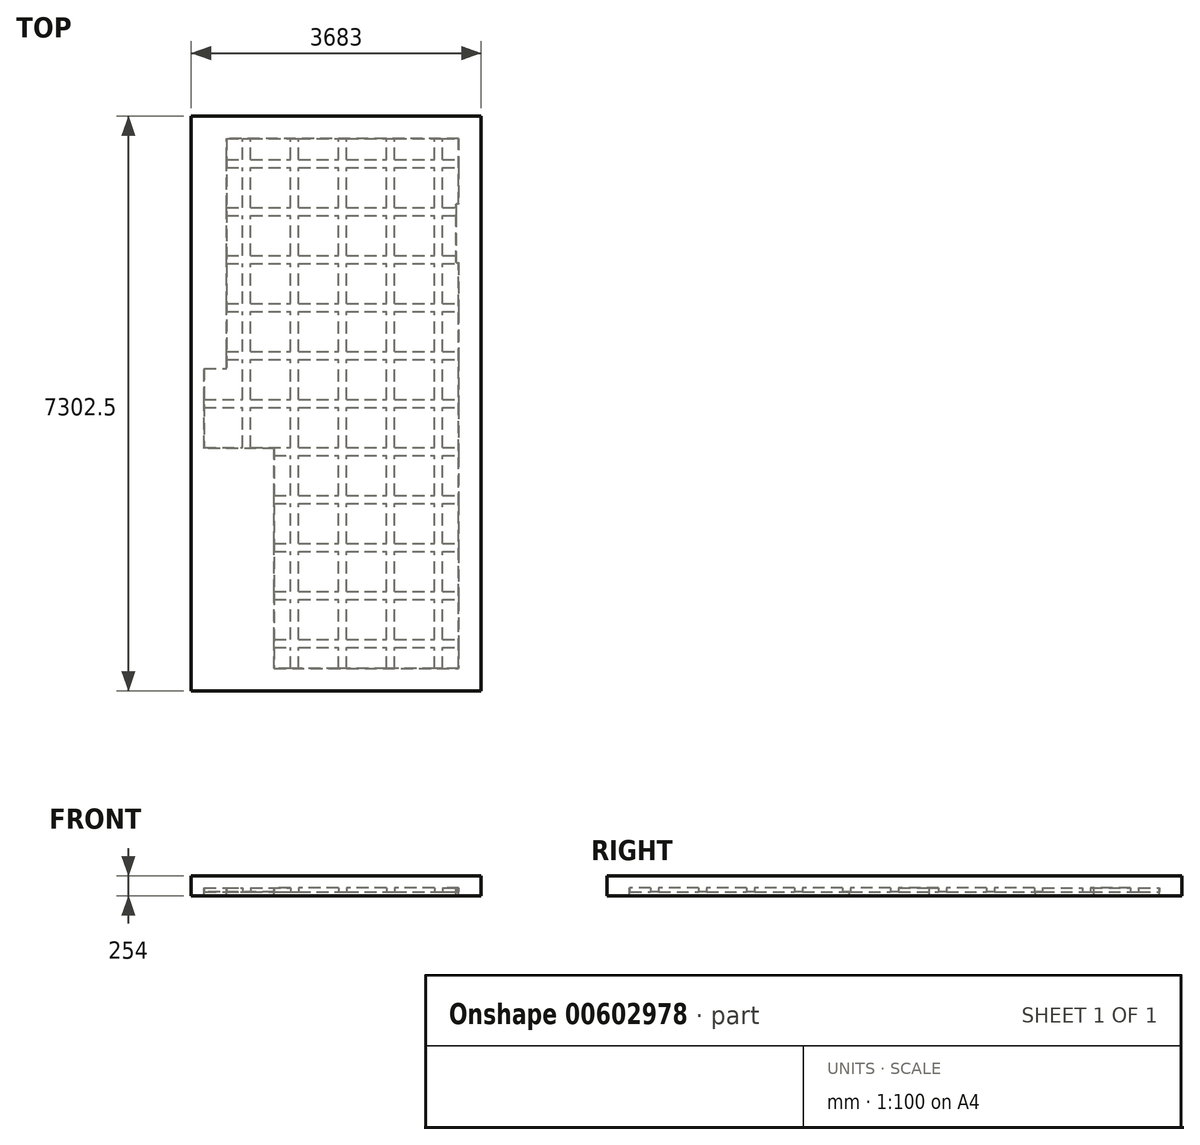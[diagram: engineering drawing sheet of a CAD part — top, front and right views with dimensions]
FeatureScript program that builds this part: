
annotation { "Feature Type Name" : "Feature", "Feature Type Description" : "" }
export const myFeature = defineFeature(function(context is Context, id is Id, definition is map)
    precondition{}
    {
        {
            var Q0;
            Q0=qCreatedBy(makeId("Top.planeOp"),FACE);
            var sketch = newSketch(context, id + "F0", { "sketchPlane" : qUnion([Q0])});
            skLineSegment(sketch, "E0", {"start": v(0, 0) * mm, "end": v(0, 5156.2) * mm});
            skLineSegment(sketch, "E1", {"start": v(0, 5156.2) * mm, "end": v(-34.92, 5156.2) * mm});
            skLineSegment(sketch, "E2", {"start": v(-34.92, 5156.2) * mm, "end": v(-34.92, 5899.15) * mm});
            skLineSegment(sketch, "E3", {"start": v(-34.92, 5899.15) * mm, "end": v(0, 5899.15) * mm});
            skLineSegment(sketch, "E4", {"start": v(0, 5899.15) * mm, "end": v(0, 6731) * mm});
            skLineSegment(sketch, "E5", {"start": v(0, 6731) * mm, "end": v(-2946.4, 6731) * mm});
            skLineSegment(sketch, "E6", {"start": v(-2946.4, 6731) * mm, "end": v(-2946.4, 3810) * mm});
            skLineSegment(sketch, "E7", {"start": v(-2946.4, 3810) * mm, "end": v(-3232.15, 3810) * mm});
            skLineSegment(sketch, "E8", {"start": v(-3232.15, 3810) * mm, "end": v(-3232.15, 2794) * mm});
            skLineSegment(sketch, "E9", {"start": v(-3232.15, 2794) * mm, "end": v(-2343.15, 2794) * mm});
            skLineSegment(sketch, "E10", {"start": v(-2343.15, 2794) * mm, "end": v(-2343.15, 0) * mm});
            skLineSegment(sketch, "E11", {"start": v(-2343.15, 0) * mm, "end": v(0, 0) * mm});
            skLineSegment(sketch, "E12", {"start": v(285.75, 7016.75) * mm, "end": v(285.75, -285.75) * mm});
            skLineSegment(sketch, "E13", {"start": v(285.75, -285.75) * mm, "end": v(-3397.25, -285.75) * mm});
            skLineSegment(sketch, "E14", {"start": v(285.75, 7016.75) * mm, "end": v(-3397.25, 7016.75) * mm});
            skLineSegment(sketch, "E15", {"start": v(-3397.25, 7016.75) * mm, "end": v(-3397.25, -285.75) * mm});
            skSolve(sketch);
        }
        {
            var Q0;
            Q0=makeQuery(id+"F0.imprint","IMPRINT",FACE,{"disambiguationData":[TD([[makeQuery(id+"F0.imprint","IMPRINT",EDGE,{"derivedFrom":sQuery(id+"F0.wireOp",EDGE,"E0")}),-1.0]])]});
            extrude(context, id + "F1", {"entities" : qUnion([Q0]), "oppositeDirection" : true, "depth" : 254 * mm, "offsetDistance" : 25.4 * mm});
        }
        {
            var Q0;
            Q0 = qSketchRegion(id + "F0", true);
            var Q1;
            Q1=makeQuery(id+"F0.imprint","IMPRINT",FACE,{"disambiguationData":[TD([[makeQuery(id+"F0.imprint","IMPRINT",EDGE,{"derivedFrom":sQuery(id+"F0.wireOp",EDGE,"E0")}),1.0]])]});
            extrude(context, id + "F2", {"entities" : qUnion([Q0, Q1]), "operationType" : NewBodyOperationType.ADD, "oppositeDirection" : true, "depth" : 203.2 * mm, "offsetDistance" : 25.4 * mm});
        }
        {
            var Q0;
            Q0=makeQuery(id+"F2.opExtrude","CAP_FACE",FACE,{"disambiguationData":[OSD([sQuery(id+"F0.wireOp",EDGE,"E12"),sQuery(id+"F0.wireOp",EDGE,"E13"),sQuery(id+"F0.wireOp",EDGE,"E14"),sQuery(id+"F0.wireOp",EDGE,"E15")])],"isStart":false});
            var sketch = newSketch(context, id + "F3", { "sketchPlane" : qUnion([Q0])});
            skLineSegment(sketch, "E16.bottom", {"start": v(-2035.18, 0) * mm, "end": v(-2136.78, 0) * mm});
            skLineSegment(sketch, "E16.top", {"start": v(-2035.18, -6731) * mm, "end": v(-2136.78, -6731) * mm});
            skLineSegment(sketch, "E16.left", {"start": v(-2035.18, 0) * mm, "end": v(-2035.18, -266.7) * mm});
            skLineSegment(sketch, "E16.right", {"start": v(-2136.78, 0) * mm, "end": v(-2136.78, -266.7) * mm});
            skLineSegment(sketch, "E17.bottom", {"start": v(-1425.58, 0) * mm, "end": v(-1527.18, 0) * mm});
            skLineSegment(sketch, "E17.top", {"start": v(-1425.58, -6731) * mm, "end": v(-1527.18, -6731) * mm});
            skLineSegment(sketch, "E17.left", {"start": v(-1425.58, 0) * mm, "end": v(-1425.58, -266.7) * mm});
            skLineSegment(sketch, "E17.right", {"start": v(-1527.18, 0) * mm, "end": v(-1527.18, -266.7) * mm});
            skPoint(sketch, "E18.oppositeSnap0", {"position": v(-917.58, 0) * mm});
            skLineSegment(sketch, "E18.bottom", {"start": v(-815.98, 0) * mm, "end": v(-917.58, 0) * mm});
            skLineSegment(sketch, "E18.top", {"start": v(-815.98, -6731) * mm, "end": v(-917.58, -6731) * mm});
            skLineSegment(sketch, "E18.left", {"start": v(-815.98, 0) * mm, "end": v(-815.98, -266.7) * mm});
            skLineSegment(sketch, "E18.right", {"start": v(-917.58, 0) * mm, "end": v(-917.58, -266.7) * mm});
            skLineSegment(sketch, "E19.bottom", {"start": v(-307.98, 0) * mm, "end": v(-206.38, 0) * mm});
            skLineSegment(sketch, "E19.top", {"start": v(-307.98, -6731) * mm, "end": v(-206.38, -6731) * mm});
            skLineSegment(sketch, "E19.left", {"start": v(-307.98, 0) * mm, "end": v(-307.98, -266.7) * mm});
            skLineSegment(sketch, "E19.right", {"start": v(-206.38, 0) * mm, "end": v(-206.38, -266.7) * mm});
            skLineSegment(sketch, "E20.bottom", {"start": v(-2746.38, -2794) * mm, "end": v(-2644.78, -2794) * mm});
            skLineSegment(sketch, "E20.top", {"start": v(-2746.38, -6731) * mm, "end": v(-2644.78, -6731) * mm});
            skLineSegment(sketch, "E20.left", {"start": v(-2746.38, -2794) * mm, "end": v(-2746.38, -3314.7) * mm});
            skLineSegment(sketch, "E20.right", {"start": v(-2644.78, -2794) * mm, "end": v(-2644.78, -3314.7) * mm});
            skLineSegment(sketch, "E21.bottom", {"start": v(-2946.4, -6362.7) * mm, "end": v(-2746.38, -6362.7) * mm});
            skLineSegment(sketch, "E21.top", {"start": v(-2946.4, -6464.3) * mm, "end": v(-2746.38, -6464.3) * mm});
            skLineSegment(sketch, "E21.left", {"start": v(-2946.4, -6362.7) * mm, "end": v(-2946.4, -6464.3) * mm});
            skLineSegment(sketch, "E21.right", {"start": v(0, -6362.7) * mm, "end": v(0, -6464.3) * mm});
            skLineSegment(sketch, "E22.bottom", {"start": v(-2946.4, -5854.7) * mm, "end": v(-2746.38, -5854.7) * mm});
            skLineSegment(sketch, "E22.top", {"start": v(-2946.4, -5753.1) * mm, "end": v(-2746.38, -5753.1) * mm});
            skLineSegment(sketch, "E22.left", {"start": v(-2946.4, -5854.7) * mm, "end": v(-2946.4, -5753.1) * mm});
            skLineSegment(sketch, "E22.right", {"start": v(-34.92, -5854.7) * mm, "end": v(-34.92, -5753.1) * mm});
            skLineSegment(sketch, "E23.bottom", {"start": v(-2946.4, -5245.1) * mm, "end": v(-2746.38, -5245.1) * mm});
            skLineSegment(sketch, "E23.top", {"start": v(-2946.4, -5143.5) * mm, "end": v(-2746.38, -5143.5) * mm});
            skLineSegment(sketch, "E23.left", {"start": v(-2946.4, -5245.1) * mm, "end": v(-2946.4, -5143.5) * mm});
            skLineSegment(sketch, "E23.right", {"start": v(0, -5245.1) * mm, "end": v(0, -5143.5) * mm});
            skLineSegment(sketch, "E24.bottom", {"start": v(-2946.4, -4533.9) * mm, "end": v(-2746.38, -4533.9) * mm});
            skLineSegment(sketch, "E24.top", {"start": v(-2946.4, -4635.5) * mm, "end": v(-2746.38, -4635.5) * mm});
            skLineSegment(sketch, "E24.left", {"start": v(-2946.4, -4533.9) * mm, "end": v(-2946.4, -4635.5) * mm});
            skLineSegment(sketch, "E24.right", {"start": v(0, -4533.9) * mm, "end": v(0, -4635.5) * mm});
            skLineSegment(sketch, "E25.bottom", {"start": v(-2946.4, -3924.3) * mm, "end": v(-2746.38, -3924.3) * mm});
            skLineSegment(sketch, "E25.top", {"start": v(-2946.4, -4025.9) * mm, "end": v(-2746.38, -4025.9) * mm});
            skLineSegment(sketch, "E25.left", {"start": v(-2946.4, -3924.3) * mm, "end": v(-2946.4, -4025.9) * mm});
            skLineSegment(sketch, "E25.right", {"start": v(0, -3924.3) * mm, "end": v(0, -4025.9) * mm});
            skLineSegment(sketch, "E26.bottom", {"start": v(-3232.15, -3314.7) * mm, "end": v(-2746.38, -3314.7) * mm});
            skLineSegment(sketch, "E26.top", {"start": v(-3232.15, -3416.3) * mm, "end": v(-2746.38, -3416.3) * mm});
            skLineSegment(sketch, "E26.left", {"start": v(-3232.15, -3314.7) * mm, "end": v(-3232.15, -3416.3) * mm});
            skLineSegment(sketch, "E26.right", {"start": v(0, -3314.7) * mm, "end": v(0, -3416.3) * mm});
            skLineSegment(sketch, "E27.bottom", {"start": v(-3232.15, -2705.1) * mm, "end": v(-2136.78, -2705.1) * mm});
            skLineSegment(sketch, "E27.top", {"start": v(-3232.15, -2806.7) * mm, "end": v(-2746.38, -2806.7) * mm});
            skLineSegment(sketch, "E27.left", {"start": v(-3232.15, -2705.1) * mm, "end": v(-3232.15, -2806.7) * mm});
            skLineSegment(sketch, "E27.right", {"start": v(0, -2705.1) * mm, "end": v(0, -2806.7) * mm});
            skLineSegment(sketch, "E28.bottom", {"start": v(-2343.15, -2095.5) * mm, "end": v(-2136.78, -2095.5) * mm});
            skLineSegment(sketch, "E28.top", {"start": v(-2343.15, -2197.1) * mm, "end": v(-2136.78, -2197.1) * mm});
            skLineSegment(sketch, "E28.left", {"start": v(-2343.15, -2095.5) * mm, "end": v(-2343.15, -2197.1) * mm});
            skLineSegment(sketch, "E28.right", {"start": v(0, -2095.5) * mm, "end": v(0, -2197.1) * mm});
            skLineSegment(sketch, "E29.bottom", {"start": v(-2343.15, -1485.9) * mm, "end": v(-2136.78, -1485.9) * mm});
            skLineSegment(sketch, "E29.top", {"start": v(-2343.15, -1587.5) * mm, "end": v(-2136.78, -1587.5) * mm});
            skLineSegment(sketch, "E29.left", {"start": v(-2343.15, -1485.9) * mm, "end": v(-2343.15, -1587.5) * mm});
            skLineSegment(sketch, "E29.right", {"start": v(0, -1485.9) * mm, "end": v(0, -1587.5) * mm});
            skLineSegment(sketch, "E30.bottom", {"start": v(-2343.15, -876.3) * mm, "end": v(-2136.78, -876.3) * mm});
            skLineSegment(sketch, "E30.top", {"start": v(-2343.15, -977.9) * mm, "end": v(-2136.78, -977.9) * mm});
            skLineSegment(sketch, "E30.left", {"start": v(-2343.15, -876.3) * mm, "end": v(-2343.15, -977.9) * mm});
            skLineSegment(sketch, "E30.right", {"start": v(0, -876.3) * mm, "end": v(0, -977.9) * mm});
            skLineSegment(sketch, "E31.bottom", {"start": v(-2343.15, -266.7) * mm, "end": v(-2136.78, -266.7) * mm});
            skLineSegment(sketch, "E31.top", {"start": v(-2343.15, -368.3) * mm, "end": v(-2136.78, -368.3) * mm});
            skLineSegment(sketch, "E31.left", {"start": v(-2343.15, -266.7) * mm, "end": v(-2343.15, -368.3) * mm});
            skLineSegment(sketch, "E31.right", {"start": v(0, -266.7) * mm, "end": v(0, -368.3) * mm});
            skLineSegment(sketch, "E32.trimOffspring", {"start": v(-2136.78, -2806.7) * mm, "end": v(-2136.78, -3314.7) * mm});
            skLineSegment(sketch, "E33.trimOffspring", {"start": v(-2035.18, -2806.7) * mm, "end": v(-2035.18, -3314.7) * mm});
            skLineSegment(sketch, "E34.trimOffspring", {"start": v(-2035.18, -2705.1) * mm, "end": v(-1527.18, -2705.1) * mm});
            skLineSegment(sketch, "E35.trimOffspring", {"start": v(-1527.18, -2806.7) * mm, "end": v(-1527.18, -3314.7) * mm});
            skLineSegment(sketch, "E36.trimOffspring", {"start": v(-1425.58, -2705.1) * mm, "end": v(0, -2705.1) * mm});
            skLineSegment(sketch, "E37.trimOffspring", {"start": v(-1425.58, -2806.7) * mm, "end": v(-1425.58, -3314.7) * mm});
            skLineSegment(sketch, "E38.trimOffspring", {"start": v(-1425.58, -2806.7) * mm, "end": v(0, -2806.7) * mm});
            skLineSegment(sketch, "E39.trimOffspring", {"start": v(-2035.18, -266.7) * mm, "end": v(-1527.18, -266.7) * mm});
            skLineSegment(sketch, "E40.trimOffspring", {"start": v(-2136.78, -368.3) * mm, "end": v(-2136.78, -876.3) * mm});
            skLineSegment(sketch, "E41.trimOffspring", {"start": v(-2035.18, -368.3) * mm, "end": v(-2035.18, -876.3) * mm});
            skLineSegment(sketch, "E42.trimOffspring", {"start": v(-2035.18, -368.3) * mm, "end": v(-1527.18, -368.3) * mm});
            skLineSegment(sketch, "E43.trimOffspring", {"start": v(-1527.18, -368.3) * mm, "end": v(-1527.18, -876.3) * mm});
            skLineSegment(sketch, "E44.trimOffspring", {"start": v(-1425.58, -266.7) * mm, "end": v(-917.58, -266.7) * mm});
            skLineSegment(sketch, "E45.trimOffspring", {"start": v(-1425.58, -368.3) * mm, "end": v(-1425.58, -876.3) * mm});
            skLineSegment(sketch, "E46.trimOffspring", {"start": v(-1425.58, -368.3) * mm, "end": v(-917.58, -368.3) * mm});
            skLineSegment(sketch, "E47.trimOffspring", {"start": v(-917.58, -368.3) * mm, "end": v(-917.58, -876.3) * mm});
            skLineSegment(sketch, "E48.trimOffspring", {"start": v(-815.98, -266.7) * mm, "end": v(-307.98, -266.7) * mm});
            skLineSegment(sketch, "E49.trimOffspring", {"start": v(-815.98, -368.3) * mm, "end": v(-307.98, -368.3) * mm});
            skLineSegment(sketch, "E50.trimOffspring", {"start": v(-815.98, -368.3) * mm, "end": v(-815.98, -876.3) * mm});
            skLineSegment(sketch, "E51.trimOffspring", {"start": v(-307.98, -368.3) * mm, "end": v(-307.98, -876.3) * mm});
            skLineSegment(sketch, "E52.trimOffspring", {"start": v(-206.37, -266.7) * mm, "end": v(0, -266.7) * mm});
            skLineSegment(sketch, "E53.trimOffspring", {"start": v(-206.38, -368.3) * mm, "end": v(-206.38, -876.3) * mm});
            skLineSegment(sketch, "E54.trimOffspring", {"start": v(-206.37, -368.3) * mm, "end": v(0, -368.3) * mm});
            skLineSegment(sketch, "E55.trimOffspring", {"start": v(-206.37, -876.3) * mm, "end": v(0, -876.3) * mm});
            skLineSegment(sketch, "E56.trimOffspring", {"start": v(-206.37, -977.9) * mm, "end": v(0, -977.9) * mm});
            skLineSegment(sketch, "E57.trimOffspring", {"start": v(-206.38, -977.9) * mm, "end": v(-206.38, -1485.9) * mm});
            skLineSegment(sketch, "E58.trimOffspring", {"start": v(-307.98, -977.9) * mm, "end": v(-307.98, -1485.9) * mm});
            skLineSegment(sketch, "E59.trimOffspring", {"start": v(-815.98, -977.9) * mm, "end": v(-815.98, -1485.9) * mm});
            skLineSegment(sketch, "E60.trimOffspring", {"start": v(-917.58, -977.9) * mm, "end": v(-917.58, -1485.9) * mm});
            skLineSegment(sketch, "E61.trimOffspring", {"start": v(-815.98, -876.3) * mm, "end": v(-307.97, -876.3) * mm});
            skLineSegment(sketch, "E62.trimOffspring", {"start": v(-815.98, -977.9) * mm, "end": v(-307.97, -977.9) * mm});
            skLineSegment(sketch, "E63.trimOffspring", {"start": v(-1425.58, -977.9) * mm, "end": v(-1425.58, -1485.9) * mm});
            skLineSegment(sketch, "E64.trimOffspring", {"start": v(-1425.58, -876.3) * mm, "end": v(-917.58, -876.3) * mm});
            skLineSegment(sketch, "E65.trimOffspring", {"start": v(-1425.58, -977.9) * mm, "end": v(-917.58, -977.9) * mm});
            skLineSegment(sketch, "E66.trimOffspring", {"start": v(-1527.18, -977.9) * mm, "end": v(-1527.18, -1485.9) * mm});
            skLineSegment(sketch, "E67.trimOffspring", {"start": v(-2035.18, -977.9) * mm, "end": v(-2035.18, -1485.9) * mm});
            skLineSegment(sketch, "E68.trimOffspring", {"start": v(-2035.18, -876.3) * mm, "end": v(-1527.18, -876.3) * mm});
            skLineSegment(sketch, "E69.trimOffspring", {"start": v(-2136.78, -977.9) * mm, "end": v(-2136.78, -1485.9) * mm});
            skLineSegment(sketch, "E70.trimOffspring", {"start": v(-2035.18, -977.9) * mm, "end": v(-1527.18, -977.9) * mm});
            skLineSegment(sketch, "E71.trimOffspring", {"start": v(-2035.18, -1485.9) * mm, "end": v(-1527.18, -1485.9) * mm});
            skLineSegment(sketch, "E72.trimOffspring", {"start": v(-2136.78, -1587.5) * mm, "end": v(-2136.78, -2095.5) * mm});
            skLineSegment(sketch, "E73.trimOffspring", {"start": v(-2035.18, -1587.5) * mm, "end": v(-2035.18, -2095.5) * mm});
            skLineSegment(sketch, "E74.trimOffspring", {"start": v(-2035.18, -1587.5) * mm, "end": v(-1527.18, -1587.5) * mm});
            skLineSegment(sketch, "E75.trimOffspring", {"start": v(-1527.18, -1587.5) * mm, "end": v(-1527.18, -2095.5) * mm});
            skLineSegment(sketch, "E76.trimOffspring", {"start": v(-1425.58, -1485.9) * mm, "end": v(-917.58, -1485.9) * mm});
            skLineSegment(sketch, "E77.trimOffspring", {"start": v(-1425.58, -1587.5) * mm, "end": v(-1425.58, -2095.5) * mm});
            skLineSegment(sketch, "E78.trimOffspring", {"start": v(-1425.58, -1587.5) * mm, "end": v(-917.58, -1587.5) * mm});
            skLineSegment(sketch, "E79.trimOffspring", {"start": v(-917.58, -1587.5) * mm, "end": v(-917.58, -2095.5) * mm});
            skLineSegment(sketch, "E80.trimOffspring", {"start": v(-815.98, -1485.9) * mm, "end": v(-307.98, -1485.9) * mm});
            skLineSegment(sketch, "E81.trimOffspring", {"start": v(-815.98, -1587.5) * mm, "end": v(-815.98, -2095.5) * mm});
            skLineSegment(sketch, "E82.trimOffspring", {"start": v(-815.98, -1587.5) * mm, "end": v(-307.98, -1587.5) * mm});
            skLineSegment(sketch, "E83.trimOffspring", {"start": v(-307.98, -1587.5) * mm, "end": v(-307.98, -2095.5) * mm});
            skLineSegment(sketch, "E84.trimOffspring", {"start": v(-206.37, -1485.9) * mm, "end": v(0, -1485.9) * mm});
            skLineSegment(sketch, "E85.trimOffspring", {"start": v(-206.38, -1587.5) * mm, "end": v(-206.38, -2095.5) * mm});
            skLineSegment(sketch, "E86.trimOffspring", {"start": v(-206.37, -1587.5) * mm, "end": v(0, -1587.5) * mm});
            skLineSegment(sketch, "E87.trimOffspring", {"start": v(-206.37, -2095.5) * mm, "end": v(0, -2095.5) * mm});
            skLineSegment(sketch, "E88.trimOffspring", {"start": v(-307.98, -2197.1) * mm, "end": v(-307.98, -3314.7) * mm});
            skLineSegment(sketch, "E89.trimOffspring", {"start": v(-206.37, -2197.1) * mm, "end": v(0, -2197.1) * mm});
            skLineSegment(sketch, "E90.trimOffspring", {"start": v(-206.38, -2197.1) * mm, "end": v(-206.38, -3314.7) * mm});
            skLineSegment(sketch, "E91.trimOffspring", {"start": v(-815.98, -2197.1) * mm, "end": v(-815.98, -3314.7) * mm});
            skLineSegment(sketch, "E92.trimOffspring", {"start": v(-815.98, -2095.5) * mm, "end": v(-307.98, -2095.5) * mm});
            skLineSegment(sketch, "E93.trimOffspring", {"start": v(-917.58, -2197.1) * mm, "end": v(-917.58, -3314.7) * mm});
            skLineSegment(sketch, "E94.trimOffspring", {"start": v(-815.98, -2197.1) * mm, "end": v(-307.98, -2197.1) * mm});
            skLineSegment(sketch, "E95.trimOffspring", {"start": v(-1425.58, -2197.1) * mm, "end": v(-1425.58, -2705.1) * mm});
            skLineSegment(sketch, "E96.trimOffspring", {"start": v(-1425.58, -2095.5) * mm, "end": v(-917.58, -2095.5) * mm});
            skLineSegment(sketch, "E97.trimOffspring", {"start": v(-1527.18, -2197.1) * mm, "end": v(-1527.18, -2705.1) * mm});
            skLineSegment(sketch, "E98.trimOffspring", {"start": v(-1425.58, -2197.1) * mm, "end": v(-917.58, -2197.1) * mm});
            skLineSegment(sketch, "E99.trimOffspring", {"start": v(-2035.18, -2197.1) * mm, "end": v(-2035.18, -2705.1) * mm});
            skLineSegment(sketch, "E100.trimOffspring", {"start": v(-2035.18, -2095.5) * mm, "end": v(-1527.18, -2095.5) * mm});
            skLineSegment(sketch, "E101.trimOffspring", {"start": v(-2136.78, -2197.1) * mm, "end": v(-2136.78, -2705.1) * mm});
            skLineSegment(sketch, "E102.trimOffspring", {"start": v(-2035.18, -2197.1) * mm, "end": v(-1527.18, -2197.1) * mm});
            skLineSegment(sketch, "E103.trimOffspring", {"start": v(-2644.78, -2806.7) * mm, "end": v(-1527.18, -2806.7) * mm});
            skLineSegment(sketch, "E104.trimOffspring", {"start": v(-2644.78, -3314.7) * mm, "end": v(-2136.78, -3314.7) * mm});
            skLineSegment(sketch, "E105.trimOffspring", {"start": v(-2746.38, -3416.3) * mm, "end": v(-2746.38, -3924.3) * mm});
            skLineSegment(sketch, "E106.trimOffspring", {"start": v(-2644.78, -3416.3) * mm, "end": v(-2644.78, -3924.3) * mm});
            skLineSegment(sketch, "E107.trimOffspring", {"start": v(-2644.78, -3416.3) * mm, "end": v(-2136.78, -3416.3) * mm});
            skLineSegment(sketch, "E108.trimOffspring", {"start": v(-2136.78, -3416.3) * mm, "end": v(-2136.78, -3924.3) * mm});
            skLineSegment(sketch, "E109.trimOffspring", {"start": v(-2035.18, -3314.7) * mm, "end": v(-1527.18, -3314.7) * mm});
            skLineSegment(sketch, "E110.trimOffspring", {"start": v(-2035.18, -3416.3) * mm, "end": v(-2035.18, -3924.3) * mm});
            skLineSegment(sketch, "E111.trimOffspring", {"start": v(-2035.18, -3416.3) * mm, "end": v(-1527.18, -3416.3) * mm});
            skLineSegment(sketch, "E112.trimOffspring", {"start": v(-1527.18, -3416.3) * mm, "end": v(-1527.18, -3924.3) * mm});
            skLineSegment(sketch, "E113.trimOffspring", {"start": v(-1425.58, -3314.7) * mm, "end": v(-917.58, -3314.7) * mm});
            skLineSegment(sketch, "E114.trimOffspring", {"start": v(-1425.58, -3416.3) * mm, "end": v(-1425.58, -3924.3) * mm});
            skLineSegment(sketch, "E115.trimOffspring", {"start": v(-1425.58, -3416.3) * mm, "end": v(-917.58, -3416.3) * mm});
            skLineSegment(sketch, "E116.trimOffspring", {"start": v(-206.38, -3416.3) * mm, "end": v(-206.38, -3924.3) * mm});
            skLineSegment(sketch, "E117.trimOffspring", {"start": v(-206.37, -3314.7) * mm, "end": v(0, -3314.7) * mm});
            skLineSegment(sketch, "E118.trimOffspring", {"start": v(-307.98, -3416.3) * mm, "end": v(-307.98, -3924.3) * mm});
            skLineSegment(sketch, "E119.trimOffspring", {"start": v(-206.37, -3416.3) * mm, "end": v(0, -3416.3) * mm});
            skLineSegment(sketch, "E120.trimOffspring", {"start": v(-815.98, -3416.3) * mm, "end": v(-815.98, -3924.3) * mm});
            skLineSegment(sketch, "E121.trimOffspring", {"start": v(-815.98, -3314.7) * mm, "end": v(-307.98, -3314.7) * mm});
            skLineSegment(sketch, "E122.trimOffspring", {"start": v(-917.58, -3416.3) * mm, "end": v(-917.58, -3924.3) * mm});
            skLineSegment(sketch, "E123.trimOffspring", {"start": v(-815.98, -3416.3) * mm, "end": v(-307.98, -3416.3) * mm});
            skLineSegment(sketch, "E124.trimOffspring", {"start": v(-206.38, -4025.9) * mm, "end": v(-206.38, -4533.9) * mm});
            skLineSegment(sketch, "E125.trimOffspring", {"start": v(-206.37, -3924.3) * mm, "end": v(0, -3924.3) * mm});
            skLineSegment(sketch, "E126.trimOffspring", {"start": v(-206.37, -4025.9) * mm, "end": v(0, -4025.9) * mm});
            skLineSegment(sketch, "E127.trimOffspring", {"start": v(-307.98, -4025.9) * mm, "end": v(-307.98, -4533.9) * mm});
            skLineSegment(sketch, "E128.trimOffspring", {"start": v(-815.98, -4025.9) * mm, "end": v(-815.98, -4533.9) * mm});
            skLineSegment(sketch, "E129.trimOffspring", {"start": v(-815.97, -3924.3) * mm, "end": v(-307.97, -3924.3) * mm});
            skLineSegment(sketch, "E130.trimOffspring", {"start": v(-917.58, -4025.9) * mm, "end": v(-917.58, -4533.9) * mm});
            skLineSegment(sketch, "E131.trimOffspring", {"start": v(-815.98, -4025.9) * mm, "end": v(-307.98, -4025.9) * mm});
            skLineSegment(sketch, "E132.trimOffspring", {"start": v(-1425.58, -4025.9) * mm, "end": v(-1425.58, -4533.9) * mm});
            skLineSegment(sketch, "E133.trimOffspring", {"start": v(-1425.58, -3924.3) * mm, "end": v(-917.58, -3924.3) * mm});
            skLineSegment(sketch, "E134.trimOffspring", {"start": v(-1527.18, -4025.9) * mm, "end": v(-1527.18, -4533.9) * mm});
            skLineSegment(sketch, "E135.trimOffspring", {"start": v(-1425.58, -4025.9) * mm, "end": v(-917.58, -4025.9) * mm});
            skLineSegment(sketch, "E136.trimOffspring", {"start": v(-2035.18, -3924.3) * mm, "end": v(-1527.18, -3924.3) * mm});
            skLineSegment(sketch, "E137.trimOffspring", {"start": v(-2035.18, -4025.9) * mm, "end": v(-2035.18, -4533.9) * mm});
            skLineSegment(sketch, "E138.trimOffspring", {"start": v(-2035.18, -4025.9) * mm, "end": v(-1527.18, -4025.9) * mm});
            skLineSegment(sketch, "E139.trimOffspring", {"start": v(-2136.78, -4025.9) * mm, "end": v(-2136.78, -4533.9) * mm});
            skLineSegment(sketch, "E140.trimOffspring", {"start": v(-2644.78, -4025.9) * mm, "end": v(-2644.78, -4533.9) * mm});
            skLineSegment(sketch, "E141.trimOffspring", {"start": v(-2644.78, -3924.3) * mm, "end": v(-2136.78, -3924.3) * mm});
            skLineSegment(sketch, "E142.trimOffspring", {"start": v(-2746.38, -4025.9) * mm, "end": v(-2746.38, -4533.9) * mm});
            skLineSegment(sketch, "E143.trimOffspring", {"start": v(-2644.78, -4025.9) * mm, "end": v(-2136.78, -4025.9) * mm});
            skLineSegment(sketch, "E144.trimOffspring", {"start": v(-2644.78, -4533.9) * mm, "end": v(-2136.78, -4533.9) * mm});
            skLineSegment(sketch, "E145.trimOffspring", {"start": v(-2746.38, -4635.5) * mm, "end": v(-2746.38, -5143.5) * mm});
            skLineSegment(sketch, "E146.trimOffspring", {"start": v(-2644.78, -4635.5) * mm, "end": v(-2644.78, -5143.5) * mm});
            skLineSegment(sketch, "E147.trimOffspring", {"start": v(-2644.78, -4635.5) * mm, "end": v(-2136.78, -4635.5) * mm});
            skLineSegment(sketch, "E148.trimOffspring", {"start": v(-2035.18, -4533.9) * mm, "end": v(-1527.18, -4533.9) * mm});
            skLineSegment(sketch, "E149.trimOffspring", {"start": v(-2136.78, -4635.5) * mm, "end": v(-2136.78, -5143.5) * mm});
            skLineSegment(sketch, "E150.trimOffspring", {"start": v(-2035.18, -4635.5) * mm, "end": v(-2035.18, -5143.5) * mm});
            skLineSegment(sketch, "E151.trimOffspring", {"start": v(-2035.18, -4635.5) * mm, "end": v(-1527.18, -4635.5) * mm});
            skLineSegment(sketch, "E152.trimOffspring", {"start": v(-1425.58, -4533.9) * mm, "end": v(-917.58, -4533.9) * mm});
            skLineSegment(sketch, "E153.trimOffspring", {"start": v(-1527.18, -4635.5) * mm, "end": v(-1527.18, -5143.5) * mm});
            skLineSegment(sketch, "E154.trimOffspring", {"start": v(-1425.58, -4635.5) * mm, "end": v(-1425.58, -5143.5) * mm});
            skLineSegment(sketch, "E155.trimOffspring", {"start": v(-1425.58, -4635.5) * mm, "end": v(-917.58, -4635.5) * mm});
            skLineSegment(sketch, "E156.trimOffspring", {"start": v(-815.98, -4533.9) * mm, "end": v(-307.98, -4533.9) * mm});
            skLineSegment(sketch, "E157.trimOffspring", {"start": v(-917.58, -4635.5) * mm, "end": v(-917.58, -5143.5) * mm});
            skLineSegment(sketch, "E158.trimOffspring", {"start": v(-815.98, -4635.5) * mm, "end": v(-307.98, -4635.5) * mm});
            skLineSegment(sketch, "E159.trimOffspring", {"start": v(-815.98, -4635.5) * mm, "end": v(-815.98, -5143.5) * mm});
            skLineSegment(sketch, "E160.trimOffspring", {"start": v(-206.37, -4533.9) * mm, "end": v(0, -4533.9) * mm});
            skLineSegment(sketch, "E161.trimOffspring", {"start": v(-307.98, -4635.5) * mm, "end": v(-307.98, -5143.5) * mm});
            skLineSegment(sketch, "E162.trimOffspring", {"start": v(-206.38, -4635.5) * mm, "end": v(-206.38, -5143.5) * mm});
            skLineSegment(sketch, "E163.trimOffspring", {"start": v(-206.37, -4635.5) * mm, "end": v(0, -4635.5) * mm});
            skLineSegment(sketch, "E164.trimOffspring", {"start": v(-2644.78, -5143.5) * mm, "end": v(-2136.78, -5143.5) * mm});
            skLineSegment(sketch, "E165.trimOffspring", {"start": v(-2746.38, -5245.1) * mm, "end": v(-2746.38, -5753.1) * mm});
            skLineSegment(sketch, "E166.trimOffspring", {"start": v(-2644.78, -5245.1) * mm, "end": v(-2136.78, -5245.1) * mm});
            skLineSegment(sketch, "E167.trimOffspring", {"start": v(-2644.78, -5245.1) * mm, "end": v(-2644.78, -5753.1) * mm});
            skLineSegment(sketch, "E168.trimOffspring", {"start": v(-2644.78, -5753.1) * mm, "end": v(-2136.78, -5753.1) * mm});
            skLineSegment(sketch, "E169.trimOffspring", {"start": v(-2746.38, -5854.7) * mm, "end": v(-2746.38, -6362.7) * mm});
            skLineSegment(sketch, "E170.trimOffspring", {"start": v(-2644.78, -5854.7) * mm, "end": v(-2136.78, -5854.7) * mm});
            skLineSegment(sketch, "E171.trimOffspring", {"start": v(-2644.78, -5854.7) * mm, "end": v(-2644.78, -6362.7) * mm});
            skLineSegment(sketch, "E172.trimOffspring", {"start": v(-2644.78, -6362.7) * mm, "end": v(-2136.78, -6362.7) * mm});
            skLineSegment(sketch, "E173.trimOffspring", {"start": v(-2746.38, -6464.3) * mm, "end": v(-2746.38, -6731) * mm});
            skLineSegment(sketch, "E174.trimOffspring", {"start": v(-2644.78, -6464.3) * mm, "end": v(-2136.78, -6464.3) * mm});
            skLineSegment(sketch, "E175.trimOffspring", {"start": v(-2644.78, -6464.3) * mm, "end": v(-2644.78, -6731) * mm});
            skLineSegment(sketch, "E176.trimOffspring", {"start": v(-2136.78, -5245.1) * mm, "end": v(-2136.78, -5753.1) * mm});
            skLineSegment(sketch, "E177.trimOffspring", {"start": v(-2035.18, -5143.5) * mm, "end": v(-1527.18, -5143.5) * mm});
            skLineSegment(sketch, "E178.trimOffspring", {"start": v(-2035.18, -5245.1) * mm, "end": v(-2035.18, -5753.1) * mm});
            skLineSegment(sketch, "E179.trimOffspring", {"start": v(-2035.18, -5245.1) * mm, "end": v(-1527.18, -5245.1) * mm});
            skLineSegment(sketch, "E180.trimOffspring", {"start": v(-2035.18, -5753.1) * mm, "end": v(-1527.18, -5753.1) * mm});
            skLineSegment(sketch, "E181.trimOffspring", {"start": v(-2136.78, -5854.7) * mm, "end": v(-2136.78, -6362.7) * mm});
            skLineSegment(sketch, "E182.trimOffspring", {"start": v(-2035.18, -5854.7) * mm, "end": v(-2035.18, -6362.7) * mm});
            skLineSegment(sketch, "E183.trimOffspring", {"start": v(-2035.18, -5854.7) * mm, "end": v(-1527.18, -5854.7) * mm});
            skLineSegment(sketch, "E184.trimOffspring", {"start": v(-2035.18, -6362.7) * mm, "end": v(-1527.18, -6362.7) * mm});
            skLineSegment(sketch, "E185.trimOffspring", {"start": v(-2136.78, -6464.3) * mm, "end": v(-2136.78, -6731) * mm});
            skLineSegment(sketch, "E186.trimOffspring", {"start": v(-2035.18, -6464.3) * mm, "end": v(-1527.18, -6464.3) * mm});
            skLineSegment(sketch, "E187.trimOffspring", {"start": v(-2035.18, -6464.3) * mm, "end": v(-2035.18, -6731) * mm});
            skLineSegment(sketch, "E188.trimOffspring", {"start": v(-1425.58, -5143.5) * mm, "end": v(-917.58, -5143.5) * mm});
            skLineSegment(sketch, "E189.trimOffspring", {"start": v(-1527.18, -5245.1) * mm, "end": v(-1527.18, -5753.1) * mm});
            skLineSegment(sketch, "E190.trimOffspring", {"start": v(-1425.58, -5245.1) * mm, "end": v(-1425.58, -5753.1) * mm});
            skLineSegment(sketch, "E191.trimOffspring", {"start": v(-1425.58, -5245.1) * mm, "end": v(-917.58, -5245.1) * mm});
            skLineSegment(sketch, "E192.trimOffspring", {"start": v(-1425.58, -5753.1) * mm, "end": v(-917.58, -5753.1) * mm});
            skLineSegment(sketch, "E193.trimOffspring", {"start": v(-1527.18, -5854.7) * mm, "end": v(-1527.18, -6362.7) * mm});
            skLineSegment(sketch, "E194.trimOffspring", {"start": v(-1425.58, -5854.7) * mm, "end": v(-1425.58, -6362.7) * mm});
            skLineSegment(sketch, "E195.trimOffspring", {"start": v(-1425.58, -5854.7) * mm, "end": v(-917.58, -5854.7) * mm});
            skLineSegment(sketch, "E196.trimOffspring", {"start": v(-1527.18, -6464.3) * mm, "end": v(-1527.18, -6731) * mm});
            skLineSegment(sketch, "E197.trimOffspring", {"start": v(-1425.58, -6464.3) * mm, "end": v(-917.58, -6464.3) * mm});
            skLineSegment(sketch, "E198.trimOffspring", {"start": v(-1425.58, -6464.3) * mm, "end": v(-1425.58, -6731) * mm});
            skLineSegment(sketch, "E199.trimOffspring", {"start": v(-1425.58, -6362.7) * mm, "end": v(-917.58, -6362.7) * mm});
            skLineSegment(sketch, "E200.trimOffspring", {"start": v(-815.98, -5143.5) * mm, "end": v(-307.98, -5143.5) * mm});
            skLineSegment(sketch, "E201.trimOffspring", {"start": v(-917.58, -5245.1) * mm, "end": v(-917.58, -5753.1) * mm});
            skLineSegment(sketch, "E202.trimOffspring", {"start": v(-815.98, -5245.1) * mm, "end": v(-815.98, -5753.1) * mm});
            skLineSegment(sketch, "E203.trimOffspring", {"start": v(-815.98, -5245.1) * mm, "end": v(-307.98, -5245.1) * mm});
            skLineSegment(sketch, "E204.trimOffspring", {"start": v(-815.98, -5753.1) * mm, "end": v(-307.98, -5753.1) * mm});
            skLineSegment(sketch, "E205.trimOffspring", {"start": v(-917.58, -5854.7) * mm, "end": v(-917.58, -6362.7) * mm});
            skLineSegment(sketch, "E206.trimOffspring", {"start": v(-815.98, -5854.7) * mm, "end": v(-307.98, -5854.7) * mm});
            skLineSegment(sketch, "E207.trimOffspring", {"start": v(-815.98, -5854.7) * mm, "end": v(-815.98, -6362.7) * mm});
            skLineSegment(sketch, "E208.trimOffspring", {"start": v(-815.98, -6362.7) * mm, "end": v(-307.98, -6362.7) * mm});
            skLineSegment(sketch, "E209.trimOffspring", {"start": v(-917.58, -6464.3) * mm, "end": v(-917.58, -6731) * mm});
            skLineSegment(sketch, "E210.trimOffspring", {"start": v(-815.98, -6464.3) * mm, "end": v(-307.98, -6464.3) * mm});
            skLineSegment(sketch, "E211.trimOffspring", {"start": v(-815.98, -6464.3) * mm, "end": v(-815.98, -6731) * mm});
            skLineSegment(sketch, "E212.trimOffspring", {"start": v(-206.37, -5143.5) * mm, "end": v(0, -5143.5) * mm});
            skLineSegment(sketch, "E213.trimOffspring", {"start": v(-307.98, -5245.1) * mm, "end": v(-307.98, -5753.1) * mm});
            skLineSegment(sketch, "E214.trimOffspring", {"start": v(-206.37, -5245.1) * mm, "end": v(0, -5245.1) * mm});
            skLineSegment(sketch, "E215.trimOffspring", {"start": v(-206.38, -5245.1) * mm, "end": v(-206.38, -5753.1) * mm});
            skLineSegment(sketch, "E216.trimOffspring", {"start": v(-206.37, -5753.1) * mm, "end": v(-34.92, -5753.1) * mm});
            skLineSegment(sketch, "E217.trimOffspring", {"start": v(-307.98, -5854.7) * mm, "end": v(-307.98, -6362.7) * mm});
            skLineSegment(sketch, "E218.trimOffspring", {"start": v(-206.38, -5854.7) * mm, "end": v(-206.38, -6362.7) * mm});
            skLineSegment(sketch, "E219.trimOffspring", {"start": v(-206.37, -5854.7) * mm, "end": v(-34.92, -5854.7) * mm});
            skLineSegment(sketch, "E220.trimOffspring", {"start": v(-206.37, -6362.7) * mm, "end": v(0, -6362.7) * mm});
            skLineSegment(sketch, "E221.trimOffspring", {"start": v(-307.98, -6464.3) * mm, "end": v(-307.98, -6731) * mm});
            skLineSegment(sketch, "E222.trimOffspring", {"start": v(-206.37, -6464.3) * mm, "end": v(0, -6464.3) * mm});
            skLineSegment(sketch, "E223.trimOffspring", {"start": v(-206.38, -6464.3) * mm, "end": v(-206.38, -6731) * mm});
            skSolve(sketch);
        }
        {
            var Q0;
            {var subQ0=sQuery(id+"F3.wireOp",EDGE,"E16.right");Q0=makeQuery(id+"F3.imprint","IMPRINT",FACE,{"disambiguationData":[TD([[makeQuery(id+"F3.imprint","IMPRINT",EDGE,{"derivedFrom":subQ0}),-1.0]])]});}
            var Q1;
            {var subQ0=sQuery(id+"F3.wireOp",EDGE,"E16.left");Q1=makeQuery(id+"F3.imprint","IMPRINT",FACE,{"disambiguationData":[TD([[makeQuery(id+"F3.imprint","IMPRINT",EDGE,{"derivedFrom":subQ0}),1.0]])]});}
            var Q2;
            {var subQ0=sQuery(id+"F3.wireOp",EDGE,"E17.left");Q2=makeQuery(id+"F3.imprint","IMPRINT",FACE,{"disambiguationData":[TD([[makeQuery(id+"F3.imprint","IMPRINT",EDGE,{"derivedFrom":subQ0}),1.0]])]});}
            var Q3;
            {var subQ0=sQuery(id+"F3.wireOp",EDGE,"E18.left");Q3=makeQuery(id+"F3.imprint","IMPRINT",FACE,{"disambiguationData":[TD([[makeQuery(id+"F3.imprint","IMPRINT",EDGE,{"derivedFrom":subQ0}),1.0]])]});}
            var Q4;
            {var subQ0=sQuery(id+"F3.wireOp",EDGE,"E19.right");Q4=makeQuery(id+"F3.imprint","IMPRINT",FACE,{"disambiguationData":[TD([[makeQuery(id+"F3.imprint","IMPRINT",EDGE,{"derivedFrom":subQ0}),1.0]])]});}
            var Q5;
            Q5=makeQuery(id+"F3.imprint","IMPRINT",FACE,{"disambiguationData":[TD([[makeQuery(id+"F3.imprint","IMPRINT",EDGE,{"derivedFrom":sQuery(id+"F3.wireOp",EDGE,"E53.trimOffspring")}),1.0]])]});
            var Q6;
            Q6=makeQuery(id+"F3.imprint","IMPRINT",FACE,{"disambiguationData":[TD([[makeQuery(id+"F3.imprint","IMPRINT",EDGE,{"derivedFrom":sQuery(id+"F3.wireOp",EDGE,"E49.trimOffspring")}),-1.0]])]});
            var Q7;
            Q7=makeQuery(id+"F3.imprint","IMPRINT",FACE,{"disambiguationData":[TD([[makeQuery(id+"F3.imprint","IMPRINT",EDGE,{"derivedFrom":sQuery(id+"F3.wireOp",EDGE,"E45.trimOffspring")}),1.0]])]});
            var Q8;
            Q8=makeQuery(id+"F3.imprint","IMPRINT",FACE,{"disambiguationData":[TD([[makeQuery(id+"F3.imprint","IMPRINT",EDGE,{"derivedFrom":sQuery(id+"F3.wireOp",EDGE,"E41.trimOffspring")}),1.0]])]});
            var Q9;
            {var subQ0=sQuery(id+"F3.wireOp",EDGE,"E30.bottom");Q9=makeQuery(id+"F3.imprint","IMPRINT",FACE,{"disambiguationData":[TD([[makeQuery(id+"F3.imprint","IMPRINT",EDGE,{"derivedFrom":subQ0}),1.0]])]});}
            var Q10;
            {var subQ0=sQuery(id+"F3.wireOp",EDGE,"E29.bottom");Q10=makeQuery(id+"F3.imprint","IMPRINT",FACE,{"disambiguationData":[TD([[makeQuery(id+"F3.imprint","IMPRINT",EDGE,{"derivedFrom":subQ0}),1.0]])]});}
            var Q11;
            Q11=makeQuery(id+"F3.imprint","IMPRINT",FACE,{"disambiguationData":[TD([[makeQuery(id+"F3.imprint","IMPRINT",EDGE,{"derivedFrom":sQuery(id+"F3.wireOp",EDGE,"E66.trimOffspring")}),-1.0]])]});
            var Q12;
            Q12=makeQuery(id+"F3.imprint","IMPRINT",FACE,{"disambiguationData":[TD([[makeQuery(id+"F3.imprint","IMPRINT",EDGE,{"derivedFrom":sQuery(id+"F3.wireOp",EDGE,"E60.trimOffspring")}),-1.0]])]});
            var Q13;
            Q13=makeQuery(id+"F3.imprint","IMPRINT",FACE,{"disambiguationData":[TD([[makeQuery(id+"F3.imprint","IMPRINT",EDGE,{"derivedFrom":sQuery(id+"F3.wireOp",EDGE,"E58.trimOffspring")}),-1.0]])]});
            var Q14;
            {var subQ0=sQuery(id+"F3.wireOp",EDGE,"E56.trimOffspring");Q14=makeQuery(id+"F3.imprint","IMPRINT",FACE,{"disambiguationData":[TD([[makeQuery(id+"F3.imprint","IMPRINT",EDGE,{"derivedFrom":subQ0}),-1.0]])]});}
            var Q15;
            Q15=makeQuery(id+"F3.imprint","IMPRINT",FACE,{"disambiguationData":[TD([[makeQuery(id+"F3.imprint","IMPRINT",EDGE,{"derivedFrom":sQuery(id+"F3.wireOp",EDGE,"E85.trimOffspring")}),1.0]])]});
            var Q16;
            Q16=makeQuery(id+"F3.imprint","IMPRINT",FACE,{"disambiguationData":[TD([[makeQuery(id+"F3.imprint","IMPRINT",EDGE,{"derivedFrom":sQuery(id+"F3.wireOp",EDGE,"E81.trimOffspring")}),1.0]])]});
            var Q17;
            Q17=makeQuery(id+"F3.imprint","IMPRINT",FACE,{"disambiguationData":[TD([[makeQuery(id+"F3.imprint","IMPRINT",EDGE,{"derivedFrom":sQuery(id+"F3.wireOp",EDGE,"E77.trimOffspring")}),1.0]])]});
            var Q18;
            Q18=makeQuery(id+"F3.imprint","IMPRINT",FACE,{"disambiguationData":[TD([[makeQuery(id+"F3.imprint","IMPRINT",EDGE,{"derivedFrom":sQuery(id+"F3.wireOp",EDGE,"E73.trimOffspring")}),1.0]])]});
            var Q19;
            {var subQ0=sQuery(id+"F3.wireOp",EDGE,"E28.bottom");Q19=makeQuery(id+"F3.imprint","IMPRINT",FACE,{"disambiguationData":[TD([[makeQuery(id+"F3.imprint","IMPRINT",EDGE,{"derivedFrom":subQ0}),1.0]])]});}
            var Q20;
            {var subQ4=sQuery(id+"F3.wireOp",EDGE,"E28.top");Q20=makeQuery(id+"F3.imprint","IMPRINT",FACE,{"disambiguationData":[TD([[makeQuery(id+"F3.imprint","IMPRINT",EDGE,{"derivedFrom":subQ4}),-1.0]])]});}
            var Q21;
            Q21=makeQuery(id+"F3.imprint","IMPRINT",FACE,{"disambiguationData":[TD([[makeQuery(id+"F3.imprint","IMPRINT",EDGE,{"derivedFrom":sQuery(id+"F3.wireOp",EDGE,"E34.trimOffspring")}),1.0]])]});
            var Q22;
            {var subQ0=sQuery(id+"F3.wireOp",EDGE,"E95.trimOffspring");Q22=makeQuery(id+"F3.imprint","IMPRINT",FACE,{"disambiguationData":[TD([[makeQuery(id+"F3.imprint","IMPRINT",EDGE,{"derivedFrom":subQ0}),1.0]])]});}
            var Q23;
            {var subQ5=sQuery(id+"F3.wireOp",EDGE,"E94.trimOffspring");Q23=makeQuery(id+"F3.imprint","IMPRINT",FACE,{"disambiguationData":[TD([[makeQuery(id+"F3.imprint","IMPRINT",EDGE,{"derivedFrom":subQ5}),-1.0]])]});}
            var Q24;
            {var subQ5=sQuery(id+"F3.wireOp",EDGE,"E89.trimOffspring");Q24=makeQuery(id+"F3.imprint","IMPRINT",FACE,{"disambiguationData":[TD([[makeQuery(id+"F3.imprint","IMPRINT",EDGE,{"derivedFrom":subQ5}),-1.0]])]});}
            var Q25;
            {var subQ5=sQuery(id+"F3.wireOp",EDGE,"E117.trimOffspring");Q25=makeQuery(id+"F3.imprint","IMPRINT",FACE,{"disambiguationData":[TD([[makeQuery(id+"F3.imprint","IMPRINT",EDGE,{"derivedFrom":subQ5}),1.0]])]});}
            var Q26;
            {var subQ5=sQuery(id+"F3.wireOp",EDGE,"E121.trimOffspring");Q26=makeQuery(id+"F3.imprint","IMPRINT",FACE,{"disambiguationData":[TD([[makeQuery(id+"F3.imprint","IMPRINT",EDGE,{"derivedFrom":subQ5}),1.0]])]});}
            var Q27;
            {var subQ0=sQuery(id+"F3.wireOp",EDGE,"E37.trimOffspring");Q27=makeQuery(id+"F3.imprint","IMPRINT",FACE,{"disambiguationData":[TD([[makeQuery(id+"F3.imprint","IMPRINT",EDGE,{"derivedFrom":subQ0}),1.0]])]});}
            var Q28;
            {var subQ0=sQuery(id+"F3.wireOp",EDGE,"E33.trimOffspring");Q28=makeQuery(id+"F3.imprint","IMPRINT",FACE,{"disambiguationData":[TD([[makeQuery(id+"F3.imprint","IMPRINT",EDGE,{"derivedFrom":subQ0}),1.0]])]});}
            var Q29;
            {var subQ4=sQuery(id+"F3.wireOp",EDGE,"E32.trimOffspring");Q29=makeQuery(id+"F3.imprint","IMPRINT",FACE,{"disambiguationData":[TD([[makeQuery(id+"F3.imprint","IMPRINT",EDGE,{"derivedFrom":subQ4}),-1.0]])]});}
            var Q30;
            {var subQ0=sQuery(id+"F3.wireOp",EDGE,"E26.bottom");Q30=makeQuery(id+"F3.imprint","IMPRINT",FACE,{"disambiguationData":[TD([[makeQuery(id+"F3.imprint","IMPRINT",EDGE,{"derivedFrom":subQ0}),1.0]])]});}
            var Q31;
            {var subQ2=sQuery(id+"F3.wireOp",EDGE,"E25.bottom");Q31=makeQuery(id+"F3.imprint","IMPRINT",FACE,{"disambiguationData":[TD([[makeQuery(id+"F3.imprint","IMPRINT",EDGE,{"derivedFrom":subQ2}),1.0]])]});}
            var Q32;
            Q32=makeQuery(id+"F3.imprint","IMPRINT",FACE,{"disambiguationData":[TD([[makeQuery(id+"F3.imprint","IMPRINT",EDGE,{"derivedFrom":sQuery(id+"F3.wireOp",EDGE,"E106.trimOffspring")}),1.0]])]});
            var Q33;
            Q33=makeQuery(id+"F3.imprint","IMPRINT",FACE,{"disambiguationData":[TD([[makeQuery(id+"F3.imprint","IMPRINT",EDGE,{"derivedFrom":sQuery(id+"F3.wireOp",EDGE,"E110.trimOffspring")}),1.0]])]});
            var Q34;
            Q34=makeQuery(id+"F3.imprint","IMPRINT",FACE,{"disambiguationData":[TD([[makeQuery(id+"F3.imprint","IMPRINT",EDGE,{"derivedFrom":sQuery(id+"F3.wireOp",EDGE,"E114.trimOffspring")}),1.0]])]});
            var Q35;
            Q35=makeQuery(id+"F3.imprint","IMPRINT",FACE,{"disambiguationData":[TD([[makeQuery(id+"F3.imprint","IMPRINT",EDGE,{"derivedFrom":sQuery(id+"F3.wireOp",EDGE,"E118.trimOffspring")}),-1.0]])]});
            var Q36;
            Q36=makeQuery(id+"F3.imprint","IMPRINT",FACE,{"disambiguationData":[TD([[makeQuery(id+"F3.imprint","IMPRINT",EDGE,{"derivedFrom":sQuery(id+"F3.wireOp",EDGE,"E116.trimOffspring")}),1.0]])]});
            var Q37;
            {var subQ0=sQuery(id+"F3.wireOp",EDGE,"E24.bottom");Q37=makeQuery(id+"F3.imprint","IMPRINT",FACE,{"disambiguationData":[TD([[makeQuery(id+"F3.imprint","IMPRINT",EDGE,{"derivedFrom":subQ0}),1.0]])]});}
            var Q38;
            Q38=makeQuery(id+"F3.imprint","IMPRINT",FACE,{"disambiguationData":[TD([[makeQuery(id+"F3.imprint","IMPRINT",EDGE,{"derivedFrom":sQuery(id+"F3.wireOp",EDGE,"E139.trimOffspring")}),-1.0]])]});
            var Q39;
            Q39=makeQuery(id+"F3.imprint","IMPRINT",FACE,{"disambiguationData":[TD([[makeQuery(id+"F3.imprint","IMPRINT",EDGE,{"derivedFrom":sQuery(id+"F3.wireOp",EDGE,"E134.trimOffspring")}),-1.0]])]});
            var Q40;
            Q40=makeQuery(id+"F3.imprint","IMPRINT",FACE,{"disambiguationData":[TD([[makeQuery(id+"F3.imprint","IMPRINT",EDGE,{"derivedFrom":sQuery(id+"F3.wireOp",EDGE,"E130.trimOffspring")}),-1.0]])]});
            var Q41;
            Q41=makeQuery(id+"F3.imprint","IMPRINT",FACE,{"disambiguationData":[TD([[makeQuery(id+"F3.imprint","IMPRINT",EDGE,{"derivedFrom":sQuery(id+"F3.wireOp",EDGE,"E127.trimOffspring")}),-1.0]])]});
            var Q42;
            Q42=makeQuery(id+"F3.imprint","IMPRINT",FACE,{"disambiguationData":[TD([[makeQuery(id+"F3.imprint","IMPRINT",EDGE,{"derivedFrom":sQuery(id+"F3.wireOp",EDGE,"E124.trimOffspring")}),1.0]])]});
            var Q43;
            Q43=makeQuery(id+"F3.imprint","IMPRINT",FACE,{"disambiguationData":[TD([[makeQuery(id+"F3.imprint","IMPRINT",EDGE,{"derivedFrom":sQuery(id+"F3.wireOp",EDGE,"E162.trimOffspring")}),1.0]])]});
            var Q44;
            Q44=makeQuery(id+"F3.imprint","IMPRINT",FACE,{"disambiguationData":[TD([[makeQuery(id+"F3.imprint","IMPRINT",EDGE,{"derivedFrom":sQuery(id+"F3.wireOp",EDGE,"E158.trimOffspring")}),-1.0]])]});
            var Q45;
            Q45=makeQuery(id+"F3.imprint","IMPRINT",FACE,{"disambiguationData":[TD([[makeQuery(id+"F3.imprint","IMPRINT",EDGE,{"derivedFrom":sQuery(id+"F3.wireOp",EDGE,"E154.trimOffspring")}),1.0]])]});
            var Q46;
            Q46=makeQuery(id+"F3.imprint","IMPRINT",FACE,{"disambiguationData":[TD([[makeQuery(id+"F3.imprint","IMPRINT",EDGE,{"derivedFrom":sQuery(id+"F3.wireOp",EDGE,"E150.trimOffspring")}),1.0]])]});
            var Q47;
            Q47=makeQuery(id+"F3.imprint","IMPRINT",FACE,{"disambiguationData":[TD([[makeQuery(id+"F3.imprint","IMPRINT",EDGE,{"derivedFrom":sQuery(id+"F3.wireOp",EDGE,"E146.trimOffspring")}),1.0]])]});
            var Q48;
            {var subQ0=sQuery(id+"F3.wireOp",EDGE,"E23.top");Q48=makeQuery(id+"F3.imprint","IMPRINT",FACE,{"disambiguationData":[TD([[makeQuery(id+"F3.imprint","IMPRINT",EDGE,{"derivedFrom":subQ0}),1.0]])]});}
            var Q49;
            {var subQ0=sQuery(id+"F3.wireOp",EDGE,"E22.top");Q49=makeQuery(id+"F3.imprint","IMPRINT",FACE,{"disambiguationData":[TD([[makeQuery(id+"F3.imprint","IMPRINT",EDGE,{"derivedFrom":subQ0}),1.0]])]});}
            var Q50;
            Q50=makeQuery(id+"F3.imprint","IMPRINT",FACE,{"disambiguationData":[TD([[makeQuery(id+"F3.imprint","IMPRINT",EDGE,{"derivedFrom":sQuery(id+"F3.wireOp",EDGE,"E166.trimOffspring")}),-1.0]])]});
            var Q51;
            Q51=makeQuery(id+"F3.imprint","IMPRINT",FACE,{"disambiguationData":[TD([[makeQuery(id+"F3.imprint","IMPRINT",EDGE,{"derivedFrom":sQuery(id+"F3.wireOp",EDGE,"E178.trimOffspring")}),1.0]])]});
            var Q52;
            Q52=makeQuery(id+"F3.imprint","IMPRINT",FACE,{"disambiguationData":[TD([[makeQuery(id+"F3.imprint","IMPRINT",EDGE,{"derivedFrom":sQuery(id+"F3.wireOp",EDGE,"E190.trimOffspring")}),1.0]])]});
            var Q53;
            Q53=makeQuery(id+"F3.imprint","IMPRINT",FACE,{"disambiguationData":[TD([[makeQuery(id+"F3.imprint","IMPRINT",EDGE,{"derivedFrom":sQuery(id+"F3.wireOp",EDGE,"E202.trimOffspring")}),1.0]])]});
            var Q54;
            {var subQ0=sQuery(id+"F3.wireOp",EDGE,"E215.trimOffspring");Q54=makeQuery(id+"F3.imprint","IMPRINT",FACE,{"disambiguationData":[TD([[makeQuery(id+"F3.imprint","IMPRINT",EDGE,{"derivedFrom":subQ0}),1.0]])]});}
            var Q55;
            Q55=makeQuery(id+"F3.imprint","IMPRINT",FACE,{"disambiguationData":[TD([[makeQuery(id+"F3.imprint","IMPRINT",EDGE,{"derivedFrom":sQuery(id+"F3.wireOp",EDGE,"E218.trimOffspring")}),1.0]])]});
            var Q56;
            Q56=makeQuery(id+"F3.imprint","IMPRINT",FACE,{"disambiguationData":[TD([[makeQuery(id+"F3.imprint","IMPRINT",EDGE,{"derivedFrom":sQuery(id+"F3.wireOp",EDGE,"E206.trimOffspring")}),-1.0]])]});
            var Q57;
            Q57=makeQuery(id+"F3.imprint","IMPRINT",FACE,{"disambiguationData":[TD([[makeQuery(id+"F3.imprint","IMPRINT",EDGE,{"derivedFrom":sQuery(id+"F3.wireOp",EDGE,"E194.trimOffspring")}),1.0]])]});
            var Q58;
            Q58=makeQuery(id+"F3.imprint","IMPRINT",FACE,{"disambiguationData":[TD([[makeQuery(id+"F3.imprint","IMPRINT",EDGE,{"derivedFrom":sQuery(id+"F3.wireOp",EDGE,"E182.trimOffspring")}),1.0]])]});
            var Q59;
            Q59=makeQuery(id+"F3.imprint","IMPRINT",FACE,{"disambiguationData":[TD([[makeQuery(id+"F3.imprint","IMPRINT",EDGE,{"derivedFrom":sQuery(id+"F3.wireOp",EDGE,"E170.trimOffspring")}),-1.0]])]});
            var Q60;
            {var subQ0=sQuery(id+"F3.wireOp",EDGE,"E21.bottom");Q60=makeQuery(id+"F3.imprint","IMPRINT",FACE,{"disambiguationData":[TD([[makeQuery(id+"F3.imprint","IMPRINT",EDGE,{"derivedFrom":subQ0}),1.0]])]});}
            var Q61;
            {var subQ0=sQuery(id+"F3.wireOp",EDGE,"E21.top");Q61=makeQuery(id+"F3.imprint","IMPRINT",FACE,{"disambiguationData":[TD([[makeQuery(id+"F3.imprint","IMPRINT",EDGE,{"derivedFrom":subQ0}),-1.0]])]});}
            var Q62;
            Q62=makeQuery(id+"F3.imprint","IMPRINT",FACE,{"disambiguationData":[TD([[makeQuery(id+"F3.imprint","IMPRINT",EDGE,{"derivedFrom":sQuery(id+"F3.wireOp",EDGE,"E174.trimOffspring")}),-1.0]])]});
            var Q63;
            Q63=makeQuery(id+"F3.imprint","IMPRINT",FACE,{"disambiguationData":[TD([[makeQuery(id+"F3.imprint","IMPRINT",EDGE,{"derivedFrom":sQuery(id+"F3.wireOp",EDGE,"E186.trimOffspring")}),-1.0]])]});
            var Q64;
            Q64=makeQuery(id+"F3.imprint","IMPRINT",FACE,{"disambiguationData":[TD([[makeQuery(id+"F3.imprint","IMPRINT",EDGE,{"derivedFrom":sQuery(id+"F3.wireOp",EDGE,"E197.trimOffspring")}),-1.0]])]});
            var Q65;
            Q65=makeQuery(id+"F3.imprint","IMPRINT",FACE,{"disambiguationData":[TD([[makeQuery(id+"F3.imprint","IMPRINT",EDGE,{"derivedFrom":sQuery(id+"F3.wireOp",EDGE,"E210.trimOffspring")}),-1.0]])]});
            var Q66;
            {var subQ0=sQuery(id+"F3.wireOp",EDGE,"E222.trimOffspring");Q66=makeQuery(id+"F3.imprint","IMPRINT",FACE,{"disambiguationData":[TD([[makeQuery(id+"F3.imprint","IMPRINT",EDGE,{"derivedFrom":subQ0}),-1.0]])]});}
            extrude(context, id + "F4", {"entities" : qUnion([Q0, Q1, Q2, Q3, Q4, Q5, Q6, Q7, Q8, Q9, Q10, Q11, Q12, Q13, Q14, Q15, Q16, Q17, Q18, Q19, Q20, Q21, Q22, Q23, Q24, Q25, Q26, Q27, Q28, Q29, Q30, Q31, Q32, Q33, Q34, Q35, Q36, Q37, Q38, Q39, Q40, Q41, Q42, Q43, Q44, Q45, Q46, Q47, Q48, Q49, Q50, Q51, Q52, Q53, Q54, Q55, Q56, Q57, Q58, Q59, Q60, Q61, Q62, Q63, Q64, Q65, Q66]), "operationType" : NewBodyOperationType.REMOVE, "oppositeDirection" : true, "depth" : 50.8 * mm, "offsetDistance" : 25.4 * mm});
        }
    });
